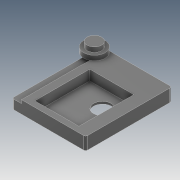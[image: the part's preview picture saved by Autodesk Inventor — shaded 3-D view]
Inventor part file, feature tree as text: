
AUTODESK INVENTOR PART (.ipt)
format: ipt  version: 2022 (Build 260153000, 153)  size: 193,024 bytes
history: native  units: mm
features: extrude x5, sketch x5, projected_geometry x4
ambient origin geometry x8: Origin, YZ Plane, XZ Plane, XY Plane, X Axis, Y Axis, Z Axis, Center Point
bodies: Volumenkörper1 (feature_tree)
feature tree (14):
  extrude  "Extrusion1"  Depth=181.5mm
  extrude  "Extrusion2"  Depth=12.0mm
  extrude  "Extrusion3"  Depth=54.0mm
  extrude  "Extrusion4"  Depth=26.5mm TaperAngle=0.0deg
  extrude  "Extrusion5"  Depth=10.0mm
  sketch  "Skizze1"  dims[d0=155.0mm d1=181.5mm]
  sketch  "Skizze2"  dims[d2=4.0mm d3=12.0mm]
  projected_geometry  "Projizierte Kontur1"
  sketch  "Skizze3"  dims[d4=26.0mm d5=54.0mm]
  sketch  "Skizze4"  dims[d6=36.0mm d7=26.5mm d8=0.0mm]
  projected_geometry  "Projizierte Kontur2"
  projected_geometry  "Projizierte Kontur3"
  sketch  "Skizze5"  dims[d9=37.5mm d11=90.5mm d12=5.0mm d13=0.0mm d14=55.0mm d15=7.3mm d16=20.0mm d17=0.0mm d18=0.0mm d19=45.0mm d20=10.0mm d21=18.0mm d22=10.0mm d23=0.0mm d24=30.0mm d25=10.0mm d26=0.0mm]
  projected_geometry  "Projizierte Kontur4"
